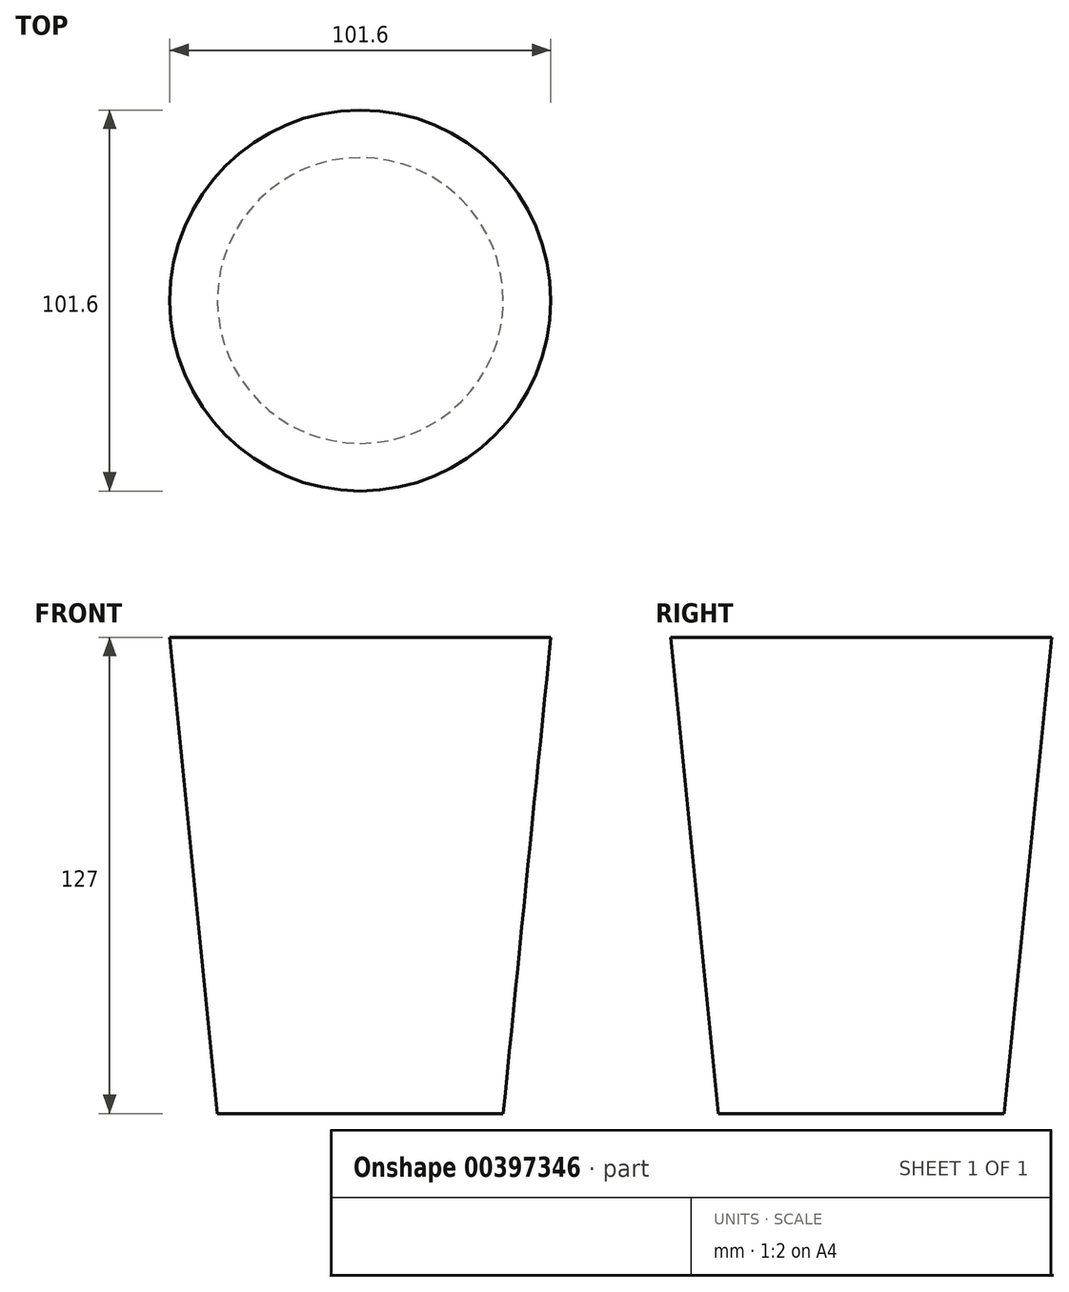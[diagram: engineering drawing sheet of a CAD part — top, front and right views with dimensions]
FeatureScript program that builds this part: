
annotation { "Feature Type Name" : "Feature", "Feature Type Description" : "" }
export const myFeature = defineFeature(function(context is Context, id is Id, definition is map)
    precondition{}
    {
        {
            var Q0;
            Q0=qCreatedBy(makeId("Top.planeOp"),FACE);
            var sketch = newSketch(context, id + "F0", { "sketchPlane" : qUnion([Q0])});
            skCircle(sketch, "E0", {"center": v(0, 0) * mm, "radius": 38.1 * mm});
            skSolve(sketch);
        }
        {
            var Q0;
            Q0=qCreatedBy(makeId("Top.planeOp"),FACE);
            cPlane(context, id + "F1", {"entities" : qUnion([Q0]), "cplaneType" : CPlaneType.OFFSET, "offset" : 127 * mm, "width" : 152.4 * mm, "height" : 152.4 * mm});
        }
        {
            var Q0;
            Q0=qCreatedBy(id+"F1.planeOp",FACE);
            var sketch = newSketch(context, id + "F2", { "sketchPlane" : qUnion([Q0])});
            skCircle(sketch, "E1", {"center": v(0, 0) * mm, "radius": 50.8 * mm});
            skSolve(sketch);
        }
        {
            var Q0;
            Q0=makeQuery(id+"F2.imprint","IMPRINT",FACE,{"disambiguationData":[TD([[makeQuery(id+"F2.imprint","IMPRINT",EDGE,{"derivedFrom":sQuery(id+"F2.wireOp",EDGE,"E1")}),1.0]])]});
            var Q1;
            Q1=makeQuery(id+"F0.imprint","IMPRINT",FACE,{"disambiguationData":[TD([[makeQuery(id+"F0.imprint","IMPRINT",EDGE,{"derivedFrom":sQuery(id+"F0.wireOp",EDGE,"E0")}),1.0]])]});
            loft(context, id + "F3", {"sheetProfilesArray" : [{ "sheetProfileEntities" : qUnion([Q0]) }, { "sheetProfileEntities" : qUnion([Q1]) }]});
        }
    });
